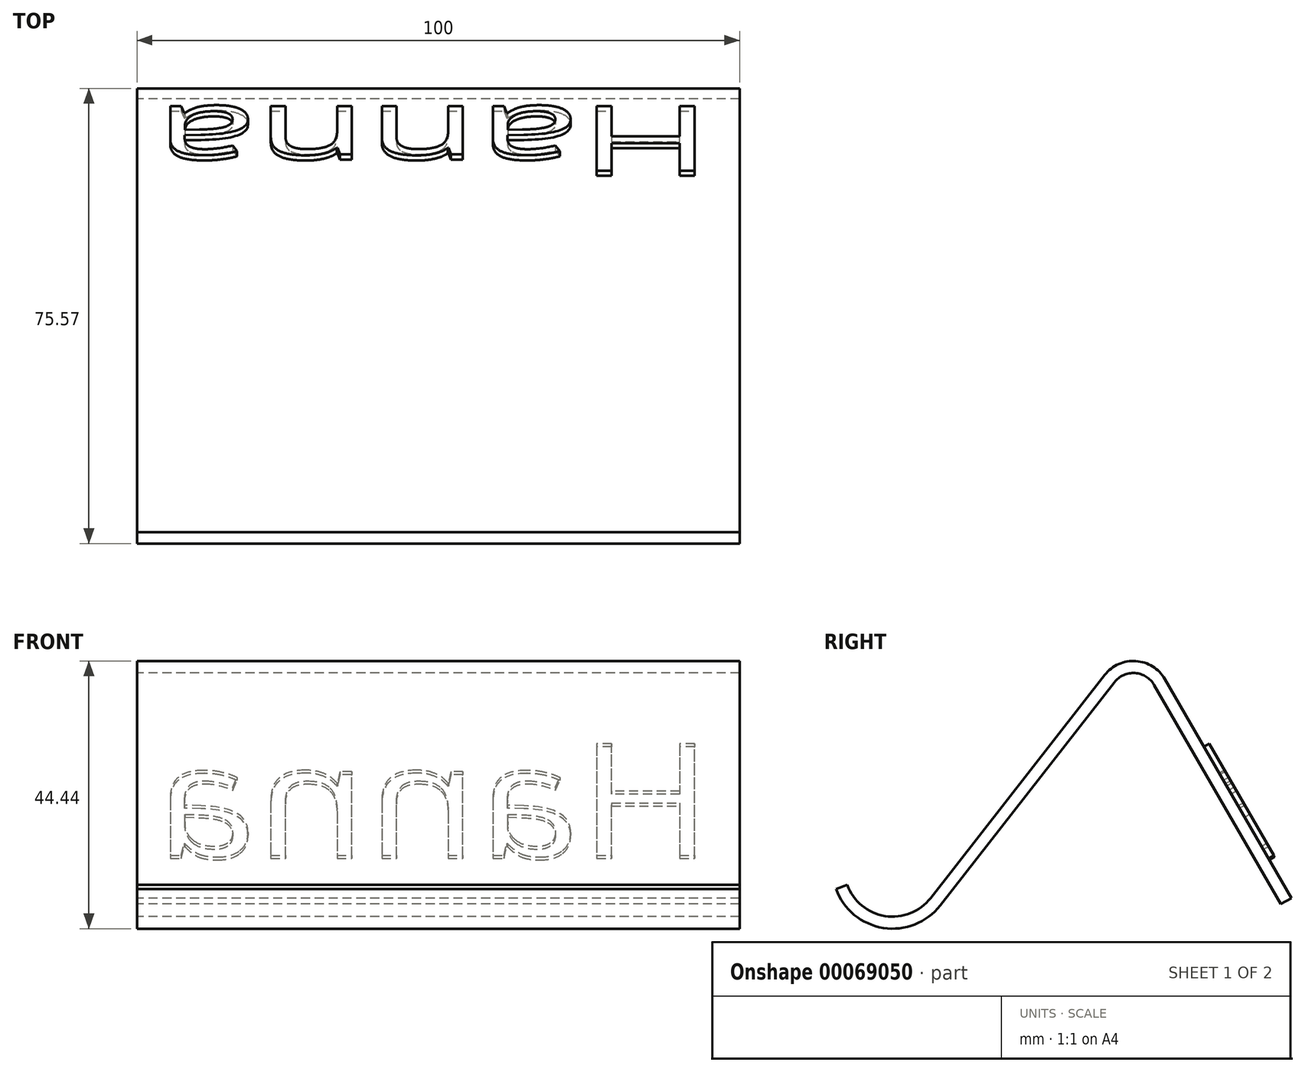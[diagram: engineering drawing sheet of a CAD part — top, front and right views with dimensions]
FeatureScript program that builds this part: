
annotation { "Feature Type Name" : "Feature", "Feature Type Description" : "" }
export const myFeature = defineFeature(function(context is Context, id is Id, definition is map)
    precondition{}
    {
        {
            var Q0;
            Q0=qCreatedBy(makeId("Right.planeOp"),FACE);
            var sketch = newSketch(context, id + "F0", { "sketchPlane" : qUnion([Q0])});
            skLineSegment(sketch, "E0", {"start": v(-5.47, 37.05) * mm, "end": v(-34.4, 0) * mm});
            skLineSegment(sketch, "E1", {"start": v(4.45, 36.36) * mm, "end": v(25.47, 0) * mm});
            skPoint(sketch, "E2.visualSharp", {"position": v(0, 44.06) * mm});
            skArc(sketch, "E2.filletArc", {"start": v(4.45, 36.36) * mm, "mid": v(-0.33, 39.35) * mm, "end": v(-5.47, 37.05) * mm});
            skArc(sketch, "E3", {"start": v(-48.22, 2.2) * mm, "mid": v(-41.95, -2.98) * mm, "end": v(-34.4, 0) * mm});
            skLineSegment(sketch, "E4.0", {"start": v(2.72, 35.36) * mm, "end": v(23.74, -1) * mm});
            skArc(sketch, "E4.1", {"start": v(2.72, 35.36) * mm, "mid": v(-0.47, 37.35) * mm, "end": v(-3.9, 35.82) * mm});
            skLineSegment(sketch, "E4.2", {"start": v(-3.9, 35.82) * mm, "end": v(-32.81, -1.23) * mm});
            skArc(sketch, "E4.3", {"start": v(-50.1, 1.51) * mm, "mid": v(-42.26, -4.95) * mm, "end": v(-32.81, -1.23) * mm});
            skLineSegment(sketch, "E5", {"start": v(-48.22, 2.2) * mm, "end": v(-50.1, 1.51) * mm});
            skLineSegment(sketch, "E6", {"start": v(23.74, -1) * mm, "end": v(25.47, 0) * mm});
            skSolve(sketch);
        }
        {
            var Q0;
            Q0=makeQuery(id+"F0.imprint","IMPRINT",FACE,{"disambiguationData":[TD([[makeQuery(id+"F0.imprint","IMPRINT",EDGE,{"derivedFrom":sQuery(id+"F0.wireOp",EDGE,"E0")}),1.0]])]});
            extrude(context, id + "F1", {"entities" : qUnion([Q0]), "depth" : 100 * mm});
        }
        {
            var Q0;
            Q0=makeQuery(id+"F1.opExtrude","SWEPT_FACE",FACE,{"disambiguationData":[OSD([sQuery(id+"F0.wireOp",EDGE,"E1")])]});
            var sketch = newSketch(context, id + "F2", { "sketchPlane" : qUnion([Q0])});
            skText(sketch, "E7", { "text": "Hanna", "fontName": "OpenSans-Regular.ttf"});
            const initialGuessF2  = {"E7": [-0.0955, -0.00516, 1, 0, 0.02162]};
            skSetInitialGuess(sketch, initialGuessF2);
            skSolve(sketch);
        }
        {
            var Q0;
            Q0 = qSketchRegion(id + "F2", true);
            extrude(context, id + "F3", {"entities" : qUnion([Q0]), "operationType" : NewBodyOperationType.ADD, "depth" : 1 * mm});
        }
    });
